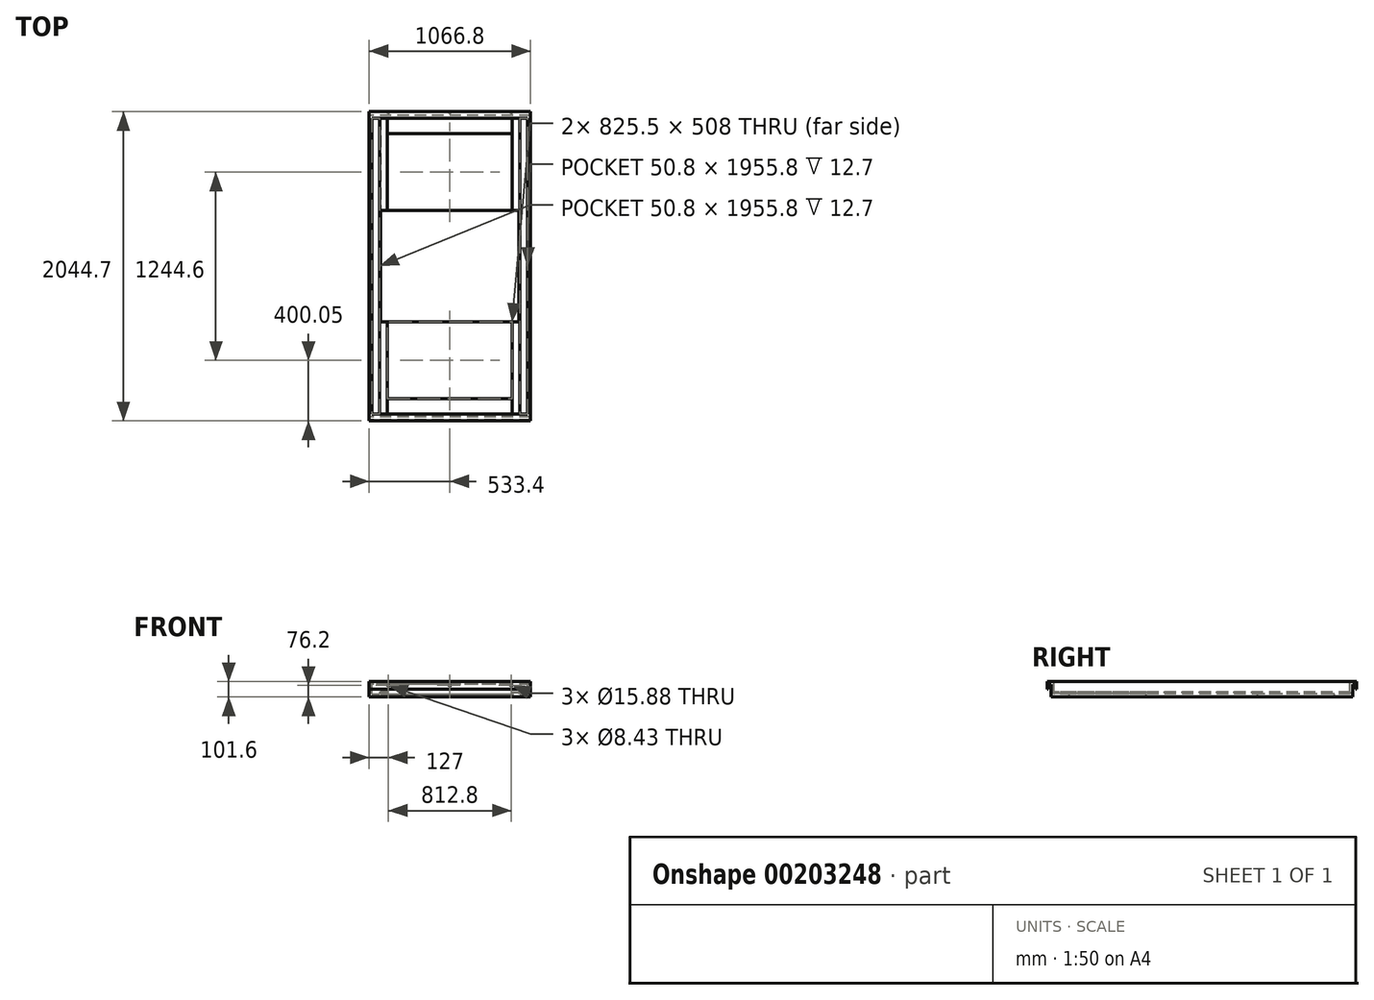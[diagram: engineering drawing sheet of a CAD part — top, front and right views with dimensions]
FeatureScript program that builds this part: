
annotation { "Feature Type Name" : "Feature", "Feature Type Description" : "" }
export const myFeature = defineFeature(function(context is Context, id is Id, definition is map)
    precondition{}
    {
        {
            var Q0;
            Q0=qCreatedBy(makeId("Top.planeOp"),FACE);
            var sketch = newSketch(context, id + "F0", { "sketchPlane" : qUnion([Q0])});
            skLineSegment(sketch, "E0.bottom", {"start": v(0, 0) * mm, "end": v(1066.8, 0) * mm});
            skLineSegment(sketch, "E0.top", {"start": v(0, 1993.9) * mm, "end": v(1066.8, 1993.9) * mm});
            skLineSegment(sketch, "E0.left", {"start": v(0, 0) * mm, "end": v(0, 1993.9) * mm});
            skLineSegment(sketch, "E0.right", {"start": v(1066.8, 0) * mm, "end": v(1066.8, 1993.9) * mm});
            skSolve(sketch);
        }
        {
            var Q0;
            Q0 = qSketchRegion(id + "F0", true);
            extrude(context, id + "F1", {"entities" : qUnion([Q0]), "depth" : 101.6 * mm});
        }
        {
            var Q0;
            Q0=makeQuery(id+"F1.opExtrude","CAP_FACE",FACE,{"disambiguationData":[OSD([sQuery(id+"F0.wireOp",EDGE,"E0.bottom"),sQuery(id+"F0.wireOp",EDGE,"E0.top"),sQuery(id+"F0.wireOp",EDGE,"E0.left"),sQuery(id+"F0.wireOp",EDGE,"E0.right")])],"isStart":false});
            var sketch = newSketch(context, id + "F2", { "sketchPlane" : qUnion([Q0])});
            skLineSegment(sketch, "E1.bottom", {"start": v(19.05, 19.05) * mm, "end": v(1047.75, 19.05) * mm});
            skLineSegment(sketch, "E1.top", {"start": v(19.05, 1974.85) * mm, "end": v(1047.75, 1974.85) * mm});
            skLineSegment(sketch, "E1.left", {"start": v(19.05, 19.05) * mm, "end": v(19.05, 1974.85) * mm});
            skLineSegment(sketch, "E1.right", {"start": v(1047.75, 19.05) * mm, "end": v(1047.75, 1974.85) * mm});
            skSolve(sketch);
        }
        {
            var Q0;
            Q0 = qSketchRegion(id + "F2", true);
            extrude(context, id + "F3", {"entities" : qUnion([Q0]), "operationType" : NewBodyOperationType.REMOVE, "oppositeDirection" : true, "depth" : 82.55 * mm});
        }
        {
            var Q0;
            Q0=makeQuery(id+"F3.boolean.opBoolean","COPY",FACE,{"derivedFrom":makeQuery(id+"F3.opExtrude","CAP_FACE",FACE,{"disambiguationData":[OSD([sQuery(id+"F2.wireOp",EDGE,"E1.bottom"),sQuery(id+"F2.wireOp",EDGE,"E1.top"),sQuery(id+"F2.wireOp",EDGE,"E1.left"),sQuery(id+"F2.wireOp",EDGE,"E1.right")])],"isStart":false})});
            var sketch = newSketch(context, id + "F4", { "sketchPlane" : qUnion([Q0])});
            skLineSegment(sketch, "E2.bottom", {"start": v(120.65, 1365.25) * mm, "end": v(946.15, 1365.25) * mm});
            skLineSegment(sketch, "E2.top", {"start": v(120.65, 1873.25) * mm, "end": v(946.15, 1873.25) * mm});
            skLineSegment(sketch, "E2.left", {"start": v(120.65, 1365.25) * mm, "end": v(120.65, 1873.25) * mm});
            skLineSegment(sketch, "E2.right", {"start": v(946.15, 1365.25) * mm, "end": v(946.15, 1873.25) * mm});
            skLineSegment(sketch, "E3.bottom", {"start": v(120.65, 628.65) * mm, "end": v(946.15, 628.65) * mm});
            skLineSegment(sketch, "E3.top", {"start": v(120.65, 120.65) * mm, "end": v(946.15, 120.65) * mm});
            skLineSegment(sketch, "E3.left", {"start": v(120.65, 628.65) * mm, "end": v(120.65, 120.65) * mm});
            skLineSegment(sketch, "E3.right", {"start": v(946.15, 628.65) * mm, "end": v(946.15, 120.65) * mm});
            skSolve(sketch);
        }
        {
            var Q0;
            Q0 = qSketchRegion(id + "F4", true);
            extrude(context, id + "F5", {"entities" : qUnion([Q0]), "operationType" : NewBodyOperationType.REMOVE, "endBound" : BoundingType.THROUGH_ALL, "oppositeDirection" : true, "depth" : 25.4 * mm});
        }
        {
            var Q0;
            Q0=makeQuery(id+"F1.opExtrude","CAP_FACE",FACE,{"disambiguationData":[OSD([sQuery(id+"F0.wireOp",EDGE,"E0.bottom"),sQuery(id+"F0.wireOp",EDGE,"E0.top"),sQuery(id+"F0.wireOp",EDGE,"E0.left"),sQuery(id+"F0.wireOp",EDGE,"E0.right")])],"isStart":false});
            var sketch = newSketch(context, id + "F6", { "sketchPlane" : qUnion([Q0])});
            skLineSegment(sketch, "E4", {"start": v(0, 1993.9) * mm, "end": v(0, 2019.3) * mm});
            skLineSegment(sketch, "E5", {"start": v(0, 2019.3) * mm, "end": v(1066.8, 2019.3) * mm});
            skLineSegment(sketch, "E6", {"start": v(1066.8, 2019.3) * mm, "end": v(1066.8, 1993.9) * mm});
            skLineSegment(sketch, "E7", {"start": v(1066.8, 1993.9) * mm, "end": v(0, 1993.9) * mm});
            skLineSegment(sketch, "E8.bottom", {"start": v(0, 0) * mm, "end": v(1066.8, 0) * mm});
            skLineSegment(sketch, "E8.top", {"start": v(0, -25.4) * mm, "end": v(1066.8, -25.4) * mm});
            skLineSegment(sketch, "E8.left", {"start": v(0, 0) * mm, "end": v(0, -25.4) * mm});
            skLineSegment(sketch, "E8.right", {"start": v(1066.8, 0) * mm, "end": v(1066.8, -25.4) * mm});
            skSolve(sketch);
        }
        {
            var Q0;
            Q0 = qSketchRegion(id + "F6", true);
            extrude(context, id + "F7", {"entities" : qUnion([Q0]), "operationType" : NewBodyOperationType.ADD, "oppositeDirection" : true, "depth" : 50.8 * mm});
        }
        {
            var Q0;
            Q0=makeQuery(id+"F7.boolean.opBoolean","MERGE",FACE,{"derivedFrom":[makeQuery(id+"F1.opExtrude","SWEPT_FACE",FACE,{"disambiguationData":[OSD([sQuery(id+"F0.wireOp",EDGE,"E0.left")])]}),makeQuery(id+"F7.opExtrude","SWEPT_FACE",FACE,{"disambiguationData":[OSD([sQuery(id+"F6.wireOp",EDGE,"E4")])]}),makeQuery(id+"F7.opExtrude","SWEPT_FACE",FACE,{"disambiguationData":[OSD([sQuery(id+"F6.wireOp",EDGE,"E8.left")])]})]});
            var sketch = newSketch(context, id + "F8", { "sketchPlane" : qUnion([Q0])});
            skLineSegment(sketch, "E9.bottom", {"start": v(-2012.95, 50.8) * mm, "end": v(-1993.9, 50.8) * mm});
            skLineSegment(sketch, "E9.top", {"start": v(-2012.95, 82.55) * mm, "end": v(-1993.9, 82.55) * mm});
            skLineSegment(sketch, "E9.left", {"start": v(-2012.95, 50.8) * mm, "end": v(-2012.95, 82.55) * mm});
            skLineSegment(sketch, "E9.right", {"start": v(-1993.9, 50.8) * mm, "end": v(-1993.9, 82.55) * mm});
            skLineSegment(sketch, "E10", {"start": v(-996.95, 101.6) * mm, "end": v(-996.95, 0) * mm, "construction": true});
            skLineSegment(sketch, "E11.MirrorCS", {"start": v(19.05, 82.55) * mm, "end": v(0, 82.55) * mm});
            skLineSegment(sketch, "E12.MirrorCS", {"start": v(0, 50.8) * mm, "end": v(0, 82.55) * mm});
            skLineSegment(sketch, "E13.MirrorCS", {"start": v(19.05, 50.8) * mm, "end": v(0, 50.8) * mm});
            skLineSegment(sketch, "E14.MirrorCS", {"start": v(19.05, 50.8) * mm, "end": v(19.05, 82.55) * mm});
            skSolve(sketch);
        }
        {
            var Q0;
            Q0 = qSketchRegion(id + "F8", true);
            extrude(context, id + "F9", {"entities" : qUnion([Q0]), "operationType" : NewBodyOperationType.REMOVE, "endBound" : BoundingType.THROUGH_ALL, "oppositeDirection" : true, "depth" : 25.4 * mm});
        }
        {
            var Q0;
            Q0=makeQuery(id+"F7.opExtrude","SWEPT_FACE",FACE,{"disambiguationData":[OSD([sQuery(id+"F6.wireOp",EDGE,"E5")])]});
            var sketch = newSketch(context, id + "F10", { "sketchPlane" : qUnion([Q0])});
            skPoint(sketch, "E15", {"position": v(-939.8, 76.2) * mm});
            skPoint(sketch, "E16", {"position": v(-127, 76.2) * mm});
            skPoint(sketch, "E17", {"position": v(-533.4, 76.2) * mm});
            skSolve(sketch);
        }
        {
            var Q0;
            Q0=sQuery(id+"F10.wireOp",VERTEX,"E15");
            var Q1;
            Q1=sQuery(id+"F10.wireOp",VERTEX,"E17");
            var Q2;
            Q2=sQuery(id+"F10.wireOp",VERTEX,"E16");
            var Q3;
            Q3=makeQuery(id+"F1.opExtrude","SWEPT_BODY",BODY,{"disambiguationData":[OSD([sQuery(id+"F0.wireOp",EDGE,"E0.bottom"),sQuery(id+"F0.wireOp",EDGE,"E0.top"),sQuery(id+"F0.wireOp",EDGE,"E0.left"),sQuery(id+"F0.wireOp",EDGE,"E0.right")])]});
            hole(context, id + "F11", {"style" : HoleStyle.SIMPLE, "endStyle" : HoleEndStyle.BLIND, "holeDiameter" : 15.88 * mm, "holeDepth" : 12.7 * mm, "startFromSketch" : true, "locations" : qUnion([Q0, Q1, Q2]), "scope" : qUnion([Q3])});
        }
        {
            var Q0;
            Q0=makeQuery(id+"F7.opExtrude","SWEPT_FACE",FACE,{"disambiguationData":[OSD([sQuery(id+"F6.wireOp",EDGE,"E8.top")])]});
            var sketch = newSketch(context, id + "F12", { "sketchPlane" : qUnion([Q0])});
            skPoint(sketch, "E18", {"position": v(127, 76.2) * mm});
            skPoint(sketch, "E19", {"position": v(939.8, 76.2) * mm});
            skPoint(sketch, "E20", {"position": v(533.4, 76.2) * mm});
            skSolve(sketch);
        }
        {
            var Q0;
            Q0=sQuery(id+"F12.wireOp",VERTEX,"E18");
            var Q1;
            Q1=sQuery(id+"F12.wireOp",VERTEX,"E20");
            var Q2;
            Q2=sQuery(id+"F12.wireOp",VERTEX,"E19");
            var Q3;
            Q3=makeQuery(id+"F1.opExtrude","SWEPT_BODY",BODY,{"disambiguationData":[OSD([sQuery(id+"F0.wireOp",EDGE,"E0.bottom"),sQuery(id+"F0.wireOp",EDGE,"E0.top"),sQuery(id+"F0.wireOp",EDGE,"E0.left"),sQuery(id+"F0.wireOp",EDGE,"E0.right")])]});
            hole(context, id + "F13", {"style" : HoleStyle.SIMPLE, "endStyle" : HoleEndStyle.BLIND, "holeDiameter" : 8.43 * mm, "holeDepth" : 12.7 * mm, "startFromSketch" : true, "locations" : qUnion([Q0, Q1, Q2]), "scope" : qUnion([Q3])});
        }
        {
            var Q0;
            Q0=makeQuery(id+"F3.boolean.opBoolean","COPY",FACE,{"derivedFrom":makeQuery(id+"F3.opExtrude","CAP_FACE",FACE,{"disambiguationData":[OSD([sQuery(id+"F2.wireOp",EDGE,"E1.bottom"),sQuery(id+"F2.wireOp",EDGE,"E1.top"),sQuery(id+"F2.wireOp",EDGE,"E1.left"),sQuery(id+"F2.wireOp",EDGE,"E1.right")])],"isStart":false})});
            var sketch = newSketch(context, id + "F14", { "sketchPlane" : qUnion([Q0])});
            skLineSegment(sketch, "E21.bottom", {"start": v(120.65, 1974.85) * mm, "end": v(69.85, 1974.85) * mm});
            skLineSegment(sketch, "E21.top", {"start": v(120.65, 19.05) * mm, "end": v(69.85, 19.05) * mm});
            skLineSegment(sketch, "E21.left", {"start": v(120.65, 1974.85) * mm, "end": v(120.65, 19.05) * mm});
            skLineSegment(sketch, "E21.right", {"start": v(69.85, 1974.85) * mm, "end": v(69.85, 19.05) * mm});
            skLineSegment(sketch, "E22", {"start": v(533.4, 1974.85) * mm, "end": v(533.4, 19.05) * mm, "construction": true});
            skLineSegment(sketch, "E23.MirrorCS", {"start": v(946.15, 19.05) * mm, "end": v(996.95, 19.05) * mm});
            skLineSegment(sketch, "E24.MirrorCS", {"start": v(946.15, 1974.85) * mm, "end": v(996.95, 1974.85) * mm});
            skLineSegment(sketch, "E25.MirrorCS", {"start": v(946.15, 1974.85) * mm, "end": v(946.15, 19.05) * mm});
            skLineSegment(sketch, "E26.MirrorCS", {"start": v(996.95, 1974.85) * mm, "end": v(996.95, 19.05) * mm});
            skSolve(sketch);
        }
        {
            var Q0;
            Q0 = qSketchRegion(id + "F14", true);
            extrude(context, id + "F15", {"entities" : qUnion([Q0]), "operationType" : NewBodyOperationType.ADD, "depth" : 12.7 * mm});
        }
        {
            var Q0;
            Q0=makeQuery(id+"F15.boolean.opBoolean","MERGE",FACE,{"derivedFrom":[makeQuery(id+"F5.boolean.opBoolean","COPY",FACE,{"derivedFrom":makeQuery(id+"F5.opExtrude","SWEPT_FACE",FACE,{"disambiguationData":[OSD([sQuery(id+"F4.wireOp",EDGE,"E2.right")])]})}),makeQuery(id+"F5.boolean.opBoolean","COPY",FACE,{"derivedFrom":makeQuery(id+"F5.opExtrude","SWEPT_FACE",FACE,{"disambiguationData":[OSD([sQuery(id+"F4.wireOp",EDGE,"E3.right")])]})}),makeQuery(id+"F15.opExtrude","SWEPT_FACE",FACE,{"disambiguationData":[OSD([sQuery(id+"F14.wireOp",EDGE,"E25.MirrorCS")])]})]});
            var sketch = newSketch(context, id + "F16", { "sketchPlane" : qUnion([Q0])});
            skLineSegment(sketch, "E27.bottom", {"start": v(-1974.85, 19.05) * mm, "end": v(-19.05, 19.05) * mm});
            skLineSegment(sketch, "E27.top", {"start": v(-1974.85, 25.4) * mm, "end": v(-19.05, 25.4) * mm});
            skLineSegment(sketch, "E27.left", {"start": v(-1974.85, 19.05) * mm, "end": v(-1974.85, 25.4) * mm});
            skLineSegment(sketch, "E27.right", {"start": v(-19.05, 19.05) * mm, "end": v(-19.05, 25.4) * mm});
            skSolve(sketch);
        }
        {
            var Q0;
            Q0 = qSketchRegion(id + "F16", true);
            extrude(context, id + "F17", {"entities" : qUnion([Q0]), "operationType" : NewBodyOperationType.REMOVE, "oppositeDirection" : true, "depth" : 44.45 * mm});
        }
        {
            var Q0;
            Q0=makeQuery(id+"F15.boolean.opBoolean","MERGE",FACE,{"derivedFrom":[makeQuery(id+"F5.boolean.opBoolean","COPY",FACE,{"derivedFrom":makeQuery(id+"F5.opExtrude","SWEPT_FACE",FACE,{"disambiguationData":[OSD([sQuery(id+"F4.wireOp",EDGE,"E2.left")])]})}),makeQuery(id+"F5.boolean.opBoolean","COPY",FACE,{"derivedFrom":makeQuery(id+"F5.opExtrude","SWEPT_FACE",FACE,{"disambiguationData":[OSD([sQuery(id+"F4.wireOp",EDGE,"E3.left")])]})}),makeQuery(id+"F15.opExtrude","SWEPT_FACE",FACE,{"disambiguationData":[OSD([sQuery(id+"F14.wireOp",EDGE,"E21.left")])]})]});
            var sketch = newSketch(context, id + "F18", { "sketchPlane" : qUnion([Q0])});
            skLineSegment(sketch, "E28.bottom", {"start": v(19.05, 19.05) * mm, "end": v(1974.85, 19.05) * mm});
            skLineSegment(sketch, "E28.top", {"start": v(19.05, 25.4) * mm, "end": v(1974.85, 25.4) * mm});
            skLineSegment(sketch, "E28.left", {"start": v(19.05, 19.05) * mm, "end": v(19.05, 25.4) * mm});
            skLineSegment(sketch, "E28.right", {"start": v(1974.85, 19.05) * mm, "end": v(1974.85, 25.4) * mm});
            skSolve(sketch);
        }
        {
            var Q0;
            Q0 = qSketchRegion(id + "F18", true);
            extrude(context, id + "F19", {"entities" : qUnion([Q0]), "operationType" : NewBodyOperationType.REMOVE, "oppositeDirection" : true, "depth" : 44.45 * mm});
        }
        {
            var Q0;
            Q0=makeQuery(id+"F15.opExtrude","CAP_FACE",FACE,{"disambiguationData":[OSD([sQuery(id+"F14.wireOp",EDGE,"E23.MirrorCS"),sQuery(id+"F14.wireOp",EDGE,"E24.MirrorCS"),sQuery(id+"F14.wireOp",EDGE,"E25.MirrorCS"),sQuery(id+"F14.wireOp",EDGE,"E26.MirrorCS")])],"isStart":false});
            var sketch = newSketch(context, id + "F20", { "sketchPlane" : qUnion([Q0])});
            skLineSegment(sketch, "E29.bottom", {"start": v(946.15, 628.65) * mm, "end": v(990.6, 628.65) * mm});
            skLineSegment(sketch, "E29.top", {"start": v(946.15, 1365.25) * mm, "end": v(990.6, 1365.25) * mm});
            skLineSegment(sketch, "E29.left", {"start": v(946.15, 628.65) * mm, "end": v(946.15, 1365.25) * mm});
            skLineSegment(sketch, "E29.right", {"start": v(990.6, 628.65) * mm, "end": v(990.6, 1365.25) * mm});
            skLineSegment(sketch, "E30", {"start": v(533.4, 1365.25) * mm, "end": v(533.4, 628.65) * mm, "construction": true});
            skLineSegment(sketch, "E31.MirrorCS", {"start": v(120.65, 628.65) * mm, "end": v(76.2, 628.65) * mm});
            skLineSegment(sketch, "E32.MirrorCS", {"start": v(120.65, 1365.25) * mm, "end": v(76.2, 1365.25) * mm});
            skLineSegment(sketch, "E33.MirrorCS", {"start": v(76.2, 628.65) * mm, "end": v(76.2, 1365.25) * mm});
            skLineSegment(sketch, "E34.MirrorCS", {"start": v(120.65, 628.65) * mm, "end": v(120.65, 1365.25) * mm});
            skSolve(sketch);
        }
        {
            var Q0;
            Q0 = qSketchRegion(id + "F20", true);
            var Q1;
            {var subQ3=sQuery(id+"F2.wireOp",EDGE,"E1.bottom");var subQ7=sQuery(id+"F2.wireOp",EDGE,"E1.top");var subQ8=makeQuery(id+"F3.boolean.opBoolean","COPY",FACE,{"derivedFrom":makeQuery(id+"F3.opExtrude","CAP_FACE",FACE,{"disambiguationData":[OSD([subQ3,subQ7,sQuery(id+"F2.wireOp",EDGE,"E1.left"),sQuery(id+"F2.wireOp",EDGE,"E1.right")])],"isStart":false})});Q1=makeQuery(id+"F19.boolean.opBoolean","MERGE",FACE,{"derivedFrom":[makeQuery(id+"F17.boolean.opBoolean","MERGE",FACE,{"derivedFrom":[makeQuery(id+"F15.boolean.opBoolean","SPLIT",FACE,{"disambiguationData":[TD([makeQuery(id+"F5.boolean.opBoolean","COPY",FACE,{"derivedFrom":makeQuery(id+"F5.opExtrude","SWEPT_FACE",FACE,{"disambiguationData":[OSD([sQuery(id+"F4.wireOp",EDGE,"E2.bottom")])]})})])],"derivedFrom":subQ8}),makeQuery(id+"F15.boolean.opBoolean","SPLIT",FACE,{"disambiguationData":[TD([makeQuery(id+"F5.boolean.opBoolean","COPY",FACE,{"derivedFrom":makeQuery(id+"F5.opExtrude","SWEPT_FACE",FACE,{"disambiguationData":[OSD([sQuery(id+"F4.wireOp",EDGE,"E2.top")])]})})])],"derivedFrom":subQ8}),makeQuery(id+"F15.boolean.opBoolean","SPLIT",FACE,{"disambiguationData":[TD([makeQuery(id+"F5.boolean.opBoolean","COPY",FACE,{"derivedFrom":makeQuery(id+"F5.opExtrude","SWEPT_FACE",FACE,{"disambiguationData":[OSD([sQuery(id+"F4.wireOp",EDGE,"E3.top")])]})})])],"derivedFrom":subQ8}),makeQuery(id+"F17.opExtrude","SWEPT_FACE",FACE,{"disambiguationData":[OSD([sQuery(id+"F16.wireOp",EDGE,"E27.bottom")])]})]}),makeQuery(id+"F19.opExtrude","SWEPT_FACE",FACE,{"disambiguationData":[OSD([sQuery(id+"F18.wireOp",EDGE,"E28.bottom")])]})]});}
            extrude(context, id + "F21", {"entities" : qUnion([Q0]), "operationType" : NewBodyOperationType.REMOVE, "endBound" : BoundingType.UP_TO_SURFACE, "oppositeDirection" : true, "endBoundEntityFace" : qUnion([Q1]), "depth" : 25.4 * mm});
        }
    });
